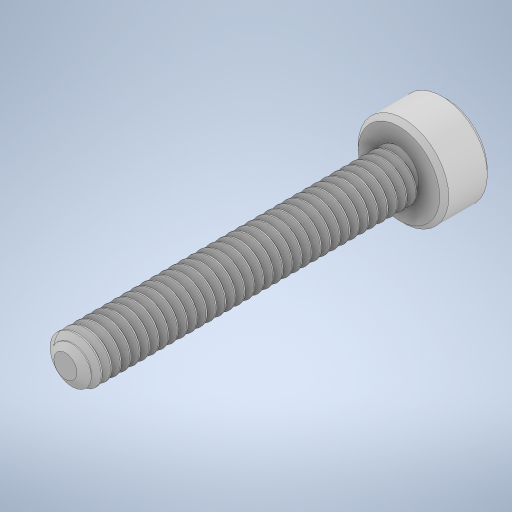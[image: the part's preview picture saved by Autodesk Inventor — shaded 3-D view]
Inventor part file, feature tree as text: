
AUTODESK INVENTOR PART (.ipt)
format: ipt  version: 2024 (Build 280153000, 153)  size: 1,203,712 bytes
history: native  units: mm
features: other x1, chamfer x1
ambient origin geometry x8: Origin, YZ Plane, XZ Plane, XY Plane, X Axis, Y Axis, Z Axis, Center Point
bodies: Body1 (feature_tree)
feature tree (2):
  other  "Těleso1"
  chamfer  "Chamfer1"  [1 undecoded]
note: 1 required parameter value undecoded (feature->parameter linkage not recoverable at this tier; creation-order binding heuristic only, values carry confidence <= 0.55)
